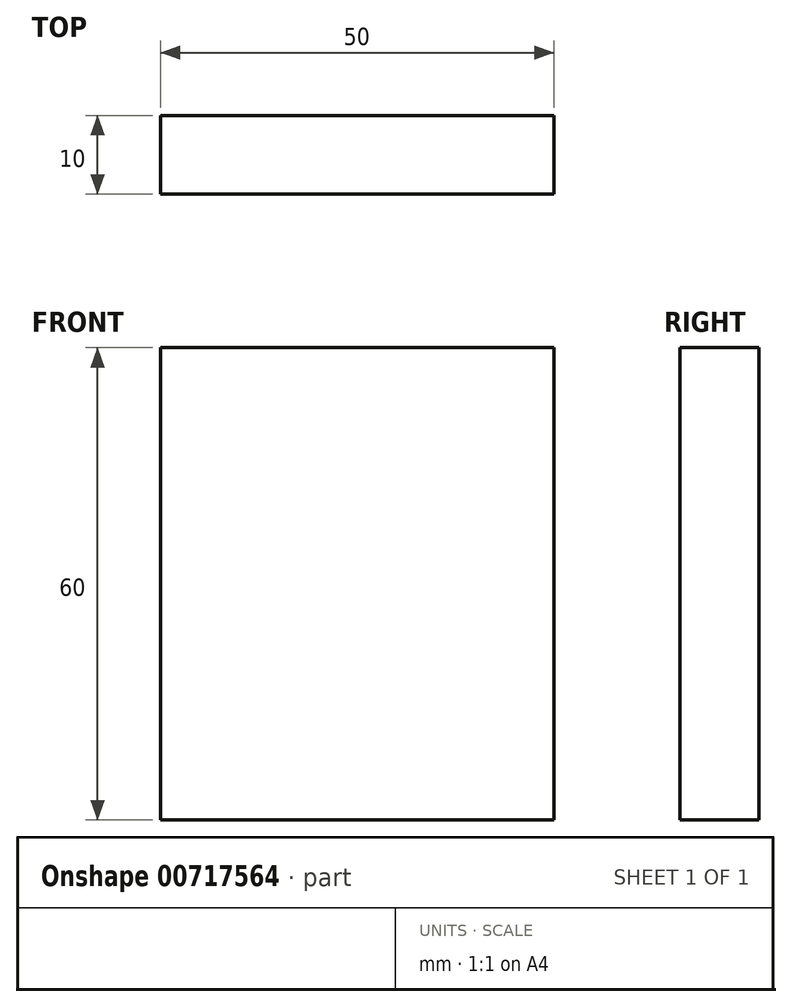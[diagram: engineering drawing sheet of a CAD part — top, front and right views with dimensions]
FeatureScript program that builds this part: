
annotation { "Feature Type Name" : "Feature", "Feature Type Description" : "" }
export const myFeature = defineFeature(function(context is Context, id is Id, definition is map)
    precondition{}
    {
        {
            var Q0;
            Q0=qCreatedBy(makeId("Front.planeOp"),FACE);
            var sketch = newSketch(context, id + "F0", { "sketchPlane" : qUnion([Q0])});
            skLineSegment(sketch, "E0.bottom", {"start": v(25, -30) * mm, "end": v(-25, -30) * mm});
            skLineSegment(sketch, "E0.top", {"start": v(25, 30) * mm, "end": v(-25, 30) * mm});
            skLineSegment(sketch, "E0.left", {"start": v(25, -30) * mm, "end": v(25, 30) * mm});
            skLineSegment(sketch, "E0.right", {"start": v(-25, -30) * mm, "end": v(-25, 30) * mm});
            skPoint(sketch, "E0.middle", {"position": v(0, 0) * mm});
            skSolve(sketch);
        }
        {
            var Q0;
            Q0 = qSketchRegion(id + "F0", true);
            extrude(context, id + "F1", {"entities" : qUnion([Q0]), "endBound" : BoundingType.SYMMETRIC, "depth" : 10 * mm, "offsetDistance" : 25 * mm});
        }
    });
